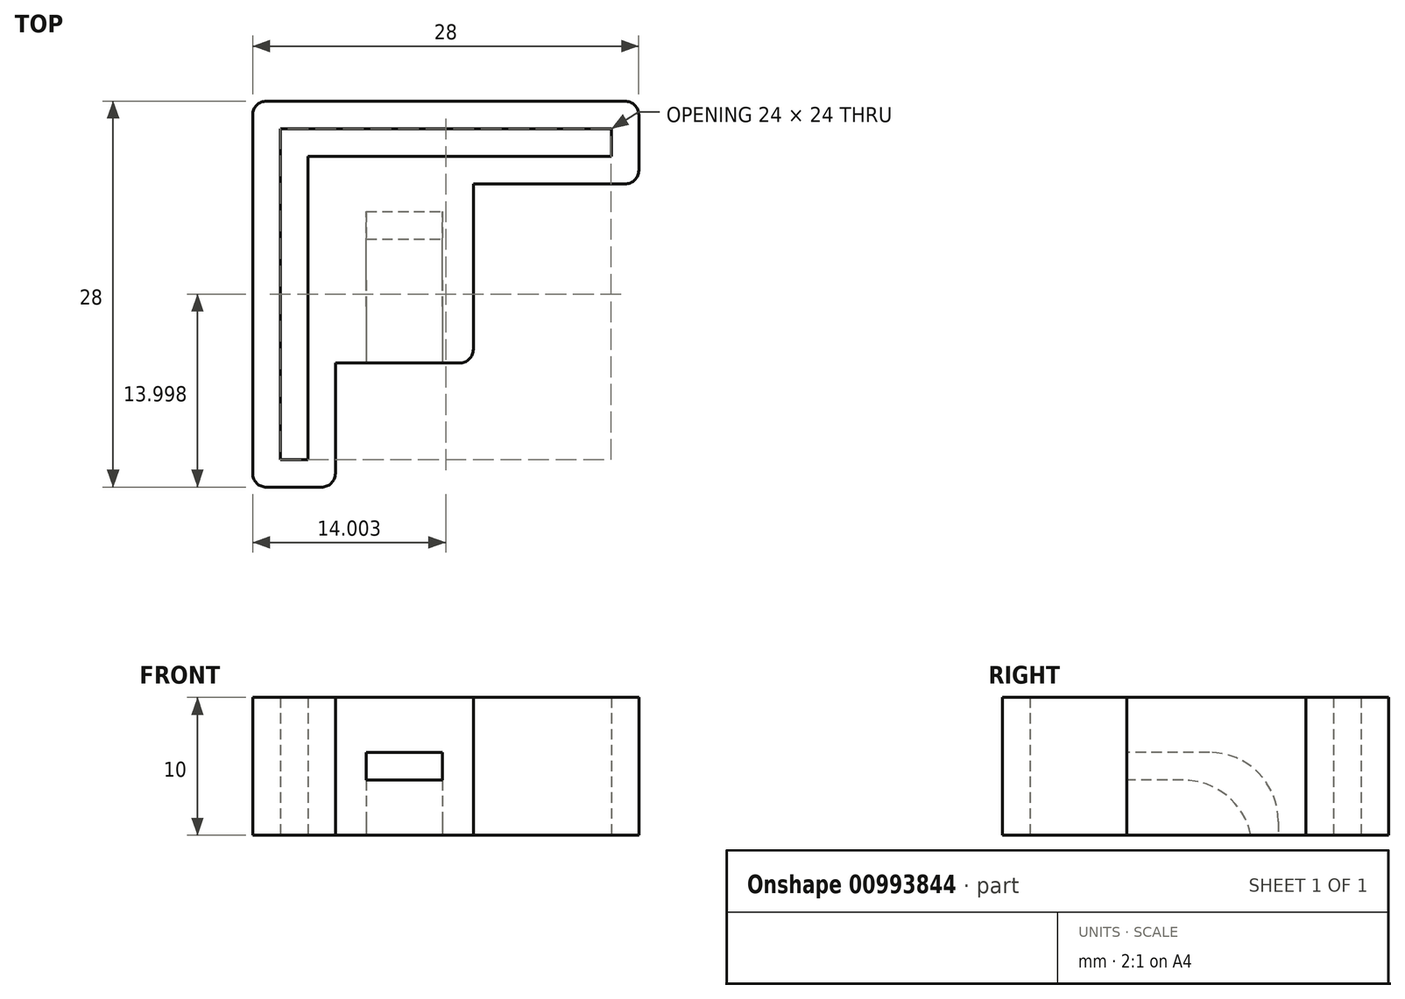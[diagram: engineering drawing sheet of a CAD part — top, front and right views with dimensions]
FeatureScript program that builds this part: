
annotation { "Feature Type Name" : "Feature", "Feature Type Description" : "" }
export const myFeature = defineFeature(function(context is Context, id is Id, definition is map)
    precondition{}
    {
        {
            var Q0;
            Q0=qCreatedBy(makeId("Top.planeOp"),FACE);
            var sketch = newSketch(context, id + "F0", { "sketchPlane" : qUnion([Q0])});
            skLineSegment(sketch, "E0", {"start": v(-10.78, -13.4) * mm, "end": v(-10.78, 10.6) * mm});
            skLineSegment(sketch, "E1", {"start": v(-10.78, 10.6) * mm, "end": v(13.22, 10.6) * mm});
            skLineSegment(sketch, "E2", {"start": v(13.22, 10.6) * mm, "end": v(13.22, 8.6) * mm});
            skLineSegment(sketch, "E3", {"start": v(13.22, 8.6) * mm, "end": v(-8.78, 8.6) * mm});
            skLineSegment(sketch, "E4", {"start": v(-8.78, 8.6) * mm, "end": v(-8.78, -13.4) * mm});
            skLineSegment(sketch, "E5", {"start": v(-8.78, -13.4) * mm, "end": v(-10.78, -13.4) * mm});
            skLineSegment(sketch, "E6", {"start": v(15.22, 6.6) * mm, "end": v(15.22, 12.6) * mm});
            skLineSegment(sketch, "E7", {"start": v(15.22, 12.6) * mm, "end": v(-12.78, 12.6) * mm});
            skLineSegment(sketch, "E8", {"start": v(-12.78, 12.6) * mm, "end": v(-12.78, -15.4) * mm});
            skLineSegment(sketch, "E9", {"start": v(-12.78, -15.4) * mm, "end": v(-6.78, -15.4) * mm});
            skLineSegment(sketch, "E10", {"start": v(-6.78, -15.4) * mm, "end": v(-6.78, 6.6) * mm});
            skLineSegment(sketch, "E11", {"start": v(-6.78, 6.6) * mm, "end": v(15.22, 6.6) * mm});
            skSolve(sketch);
        }
        {
            var Q0;
            Q0=makeQuery(id+"F0.imprint","IMPRINT",FACE,{"disambiguationData":[TD([[makeQuery(id+"F0.imprint","IMPRINT",EDGE,{"derivedFrom":sQuery(id+"F0.wireOp",EDGE,"E0")}),1.0]])]});
            extrude(context, id + "F1", {"entities" : qUnion([Q0]), "depth" : 10 * mm, "offsetDistance" : 25 * mm, "symmetric" : true});
        }
        {
            var Q0;
            Q0=makeQuery(id+"F1.opExtrude","SWEPT_FACE",FACE,{"disambiguationData":[OSD([sQuery(id+"F0.wireOp",EDGE,"E11")])]});
            var sketch = newSketch(context, id + "F2", { "sketchPlane" : qUnion([Q0])});
            skLineSegment(sketch, "E12.bottom", {"start": v(-6.78, 5) * mm, "end": v(3.22, 5) * mm});
            skLineSegment(sketch, "E12.top", {"start": v(-6.78, -5) * mm, "end": v(3.22, -5) * mm});
            skLineSegment(sketch, "E12.left", {"start": v(-6.78, 5) * mm, "end": v(-6.78, -5) * mm});
            skLineSegment(sketch, "E12.right", {"start": v(3.22, 5) * mm, "end": v(3.22, -5) * mm});
            skSolve(sketch);
        }
        {
            var Q0;
            Q0=makeQuery(id+"F2.imprint","IMPRINT",FACE,{"disambiguationData":[TD([[makeQuery(id+"F2.imprint","IMPRINT",EDGE,{"derivedFrom":sQuery(id+"F2.wireOp",EDGE,"E12.bottom")}),-1.0]])]});
            extrude(context, id + "F3", {"entities" : qUnion([Q0]), "operationType" : NewBodyOperationType.ADD, "depth" : 13 * mm, "offsetDistance" : 25 * mm});
        }
        {
            var Q0;
            Q0=makeQuery(id+"F3.opExtrude","CAP_EDGE",EDGE,{"disambiguationData":[OSD([sQuery(id+"F2.wireOp",EDGE,"E12.right")])],"isStart":true});
            var Q1;
            Q1=makeQuery(id+"F3.opExtrude","CAP_EDGE",EDGE,{"disambiguationData":[OSD([sQuery(id+"F2.wireOp",EDGE,"E12.top")])],"isStart":true});
            var Q2;
            Q2=makeQuery(id+"F3.opExtrude","CAP_EDGE",EDGE,{"disambiguationData":[OSD([sQuery(id+"F2.wireOp",EDGE,"E12.bottom")])],"isStart":true});
            var Q3;
            Q3=makeQuery(id+"F1.opExtrude","SWEPT_EDGE",EDGE,{"disambiguationData":[OSD([sQuery(id+"F0.wireOp",EDGE,"E7"),sQuery(id+"F0.wireOp",EDGE,"E8")])]});
            var Q4;
            Q4=makeQuery(id+"F1.opExtrude","SWEPT_EDGE",EDGE,{"disambiguationData":[OSD([sQuery(id+"F0.wireOp",EDGE,"E6"),sQuery(id+"F0.wireOp",EDGE,"E7")])]});
            var Q5;
            Q5=makeQuery(id+"F1.opExtrude","SWEPT_EDGE",EDGE,{"disambiguationData":[OSD([sQuery(id+"F0.wireOp",EDGE,"E6"),sQuery(id+"F0.wireOp",EDGE,"E11")])]});
            var Q6;
            Q6=makeQuery(id+"F1.opExtrude","SWEPT_EDGE",EDGE,{"disambiguationData":[OSD([sQuery(id+"F0.wireOp",EDGE,"E8"),sQuery(id+"F0.wireOp",EDGE,"E9")])]});
            var Q7;
            Q7=makeQuery(id+"F1.opExtrude","SWEPT_EDGE",EDGE,{"disambiguationData":[OSD([sQuery(id+"F0.wireOp",EDGE,"E9"),sQuery(id+"F0.wireOp",EDGE,"E10")])]});
            var Q8;
            Q8=makeQuery(id+"F3.opExtrude","CAP_EDGE",EDGE,{"disambiguationData":[OSD([sQuery(id+"F2.wireOp",EDGE,"E12.right")])],"isStart":false});
            var Q9;
            Q9=makeQuery(id+"F3.opExtrude","CAP_EDGE",EDGE,{"disambiguationData":[OSD([sQuery(id+"F2.wireOp",EDGE,"E12.left")])],"isStart":false});
            fillet(context, id + "F4", {"entities" : qUnion([Q0, Q1, Q2, Q3, Q4, Q5, Q6, Q7, Q8, Q9]), "radius" : 1 * mm, "defaultsChanged" : false, "vertexSettings" : [], "allowEdgeOverflow" : false});
        }
        {
            var Q0;
            Q0=makeQuery(id+"F3.opExtrude","CAP_FACE",FACE,{"disambiguationData":[OSD([sQuery(id+"F2.wireOp",EDGE,"E12.bottom"),sQuery(id+"F2.wireOp",EDGE,"E12.top"),sQuery(id+"F2.wireOp",EDGE,"E12.left"),sQuery(id+"F2.wireOp",EDGE,"E12.right")])],"isStart":false});
            var sketch = newSketch(context, id + "F5", { "sketchPlane" : qUnion([Q0])});
            skLineSegment(sketch, "E13.bottom", {"start": v(-4.53, 1) * mm, "end": v(0.97, 1) * mm});
            skLineSegment(sketch, "E13.top", {"start": v(-4.53, -1) * mm, "end": v(0.97, -1) * mm});
            skLineSegment(sketch, "E13.left", {"start": v(-4.53, 1) * mm, "end": v(-4.53, -1) * mm});
            skLineSegment(sketch, "E13.right", {"start": v(0.97, 1) * mm, "end": v(0.97, -1) * mm});
            skSolve(sketch);
        }
        {
            var Q0;
            Q0=makeQuery(id+"F3.boolean.opBoolean","MERGE",FACE,{"derivedFrom":[makeQuery(id+"F1.opExtrude","CAP_FACE",FACE,{"disambiguationData":[OSD([sQuery(id+"F0.wireOp",EDGE,"E0"),sQuery(id+"F0.wireOp",EDGE,"E1"),sQuery(id+"F0.wireOp",EDGE,"E2"),sQuery(id+"F0.wireOp",EDGE,"E3"),sQuery(id+"F0.wireOp",EDGE,"E4"),sQuery(id+"F0.wireOp",EDGE,"E5"),sQuery(id+"F0.wireOp",EDGE,"E6"),sQuery(id+"F0.wireOp",EDGE,"E7"),sQuery(id+"F0.wireOp",EDGE,"E8"),sQuery(id+"F0.wireOp",EDGE,"E9"),sQuery(id+"F0.wireOp",EDGE,"E10"),sQuery(id+"F0.wireOp",EDGE,"E11")])],"isStart":true}),makeQuery(id+"F3.opExtrude","SWEPT_FACE",FACE,{"disambiguationData":[OSD([sQuery(id+"F2.wireOp",EDGE,"E12.top")])]})]});
            var sketch = newSketch(context, id + "F6", { "sketchPlane" : qUnion([Q0])});
            skLineSegment(sketch, "E14.bottom", {"start": v(-4.53, -4.6) * mm, "end": v(0.97, -4.6) * mm});
            skLineSegment(sketch, "E14.top", {"start": v(-4.53, -2.6) * mm, "end": v(0.97, -2.6) * mm});
            skLineSegment(sketch, "E14.left", {"start": v(-4.53, -4.6) * mm, "end": v(-4.53, -2.6) * mm});
            skLineSegment(sketch, "E14.right", {"start": v(0.97, -4.6) * mm, "end": v(0.97, -2.6) * mm});
            skSolve(sketch);
        }
        {
            var Q0;
            Q0=makeQuery(id+"F5.imprint","IMPRINT",FACE,{"disambiguationData":[TD([[makeQuery(id+"F5.imprint","IMPRINT",EDGE,{"derivedFrom":sQuery(id+"F5.wireOp",EDGE,"E13.bottom")}),-1.0]])]});
            extrude(context, id + "F7", {"entities" : qUnion([Q0]), "operationType" : NewBodyOperationType.REMOVE, "oppositeDirection" : true, "depth" : 11 * mm, "offsetDistance" : 25 * mm});
        }
        {
            var Q0;
            Q0=makeQuery(id+"F6.imprint","IMPRINT",FACE,{"disambiguationData":[TD([[makeQuery(id+"F6.imprint","IMPRINT",EDGE,{"derivedFrom":sQuery(id+"F6.wireOp",EDGE,"E14.bottom")}),1.0]])]});
            var Q1;
            Q1=makeQuery(id+"F7.boolean.opBoolean","COPY",FACE,{"derivedFrom":makeQuery(id+"F7.opExtrude","SWEPT_FACE",FACE,{"disambiguationData":[OSD([sQuery(id+"F5.wireOp",EDGE,"E13.bottom")])]})});
            extrude(context, id + "F8", {"entities" : qUnion([Q0]), "operationType" : NewBodyOperationType.REMOVE, "endBound" : BoundingType.UP_TO_SURFACE, "oppositeDirection" : true, "depth" : 25 * mm, "endBoundEntityFace" : qUnion([Q1]), "offsetDistance" : 25 * mm});
        }
        {
            var Q0;
            Q0=makeQuery(id+"F7.boolean.opBoolean","COPY",EDGE,{"derivedFrom":makeQuery(id+"F7.opExtrude","CAP_EDGE",EDGE,{"disambiguationData":[OSD([sQuery(id+"F5.wireOp",EDGE,"E13.bottom")])],"isStart":false})});
            var Q1;
            Q1=makeQuery(id+"F8.boolean.opBoolean","INTERSECT",EDGE,{"derivedFrom":[makeQuery(id+"F7.boolean.opBoolean","COPY",FACE,{"derivedFrom":makeQuery(id+"F7.opExtrude","SWEPT_FACE",FACE,{"disambiguationData":[OSD([sQuery(id+"F5.wireOp",EDGE,"E13.top")])]})}),makeQuery(id+"F8.opExtrude","SWEPT_FACE",FACE,{"disambiguationData":[OSD([sQuery(id+"F6.wireOp",EDGE,"E14.top")])]})]});
            fillet(context, id + "F9", {"entities" : qUnion([Q0, Q1]), "tangentPropagation" : true, "radius" : 5 * mm, "defaultsChanged" : true, "vertexSettings" : [], "allowEdgeOverflow" : false});
        }
    });
